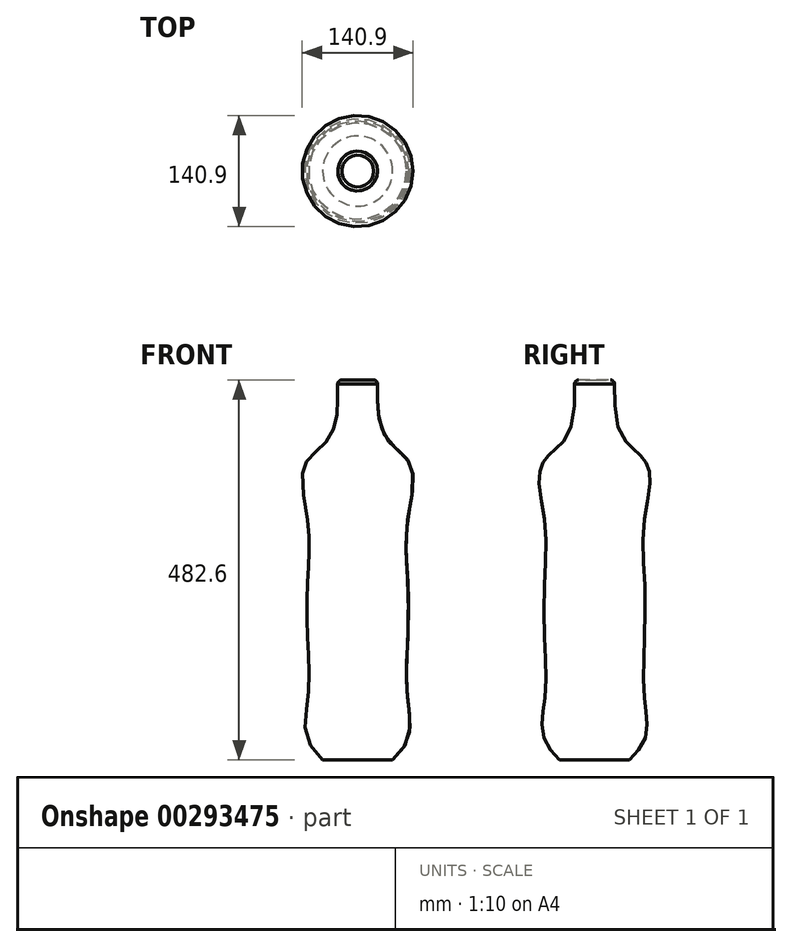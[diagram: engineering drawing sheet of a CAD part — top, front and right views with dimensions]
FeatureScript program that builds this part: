
annotation { "Feature Type Name" : "Feature", "Feature Type Description" : "" }
export const myFeature = defineFeature(function(context is Context, id is Id, definition is map)
    precondition{}
    {
        {
            var Q0;
            Q0=qCreatedBy(makeId("Top.planeOp"),FACE);
            cPlane(context, id + "F0", {"entities" : qUnion([Q0]), "cplaneType" : CPlaneType.OFFSET, "offset" : 76.2 * mm, "width" : 152.4 * mm, "height" : 152.4 * mm});
        }
        {
            var Q0;
            Q0=qCreatedBy(makeId("Top.planeOp"),FACE);
            cPlane(context, id + "F1", {"entities" : qUnion([Q0]), "cplaneType" : CPlaneType.OFFSET, "offset" : 228.6 * mm, "width" : 152.4 * mm, "height" : 152.4 * mm});
        }
        {
            var Q0;
            Q0=qCreatedBy(makeId("Top.planeOp"),FACE);
            cPlane(context, id + "F2", {"entities" : qUnion([Q0]), "cplaneType" : CPlaneType.OFFSET, "offset" : 152.4 * mm, "width" : 152.4 * mm, "height" : 152.4 * mm});
        }
        {
            var Q0;
            Q0=qCreatedBy(makeId("Top.planeOp"),FACE);
            cPlane(context, id + "F3", {"entities" : qUnion([Q0]), "cplaneType" : CPlaneType.OFFSET, "offset" : 304.8 * mm, "width" : 152.4 * mm, "height" : 152.4 * mm});
        }
        {
            var Q0;
            Q0=qCreatedBy(makeId("Top.planeOp"),FACE);
            cPlane(context, id + "F4", {"entities" : qUnion([Q0]), "cplaneType" : CPlaneType.OFFSET, "offset" : 381 * mm, "width" : 152.4 * mm, "height" : 152.4 * mm});
        }
        {
            var Q0;
            Q0=qCreatedBy(id+"F4.planeOp",FACE);
            cPlane(context, id + "F5", {"entities" : qUnion([Q0]), "cplaneType" : CPlaneType.OFFSET, "offset" : 76.2 * mm, "width" : 152.4 * mm, "height" : 152.4 * mm});
        }
        {
            var Q0;
            Q0=qCreatedBy(id+"F5.planeOp",FACE);
            cPlane(context, id + "F6", {"entities" : qUnion([Q0]), "cplaneType" : CPlaneType.OFFSET, "offset" : 76.2 * mm, "width" : 152.4 * mm, "height" : 152.4 * mm});
        }
        {
            var Q0;
            Q0=qCreatedBy(id+"F6.planeOp",FACE);
            cPlane(context, id + "F7", {"entities" : qUnion([Q0]), "cplaneType" : CPlaneType.OFFSET, "offset" : 76.2 * mm, "width" : 152.4 * mm, "height" : 152.4 * mm});
        }
        {
            var Q0;
            Q0=qCreatedBy(makeId("Top.planeOp"),FACE);
            cPlane(context, id + "F8", {"entities" : qUnion([Q0]), "cplaneType" : CPlaneType.OFFSET, "offset" : 25.4 * mm, "width" : 152.4 * mm, "height" : 152.4 * mm});
        }
        {
            var Q0;
            Q0=qCreatedBy(id+"F4.planeOp",FACE);
            cPlane(context, id + "F9", {"entities" : qUnion([Q0]), "cplaneType" : CPlaneType.OFFSET, "offset" : 25.4 * mm, "width" : 152.4 * mm, "height" : 152.4 * mm});
        }
        {
            var Q0;
            Q0=qCreatedBy(id+"F5.planeOp",FACE);
            cPlane(context, id + "F10", {"entities" : qUnion([Q0]), "cplaneType" : CPlaneType.OFFSET, "offset" : 25.4 * mm, "width" : 152.4 * mm, "height" : 152.4 * mm});
        }
        {
            var Q0;
            Q0=qCreatedBy(makeId("Top.planeOp"),FACE);
            var sketch = newSketch(context, id + "F11", { "sketchPlane" : qUnion([Q0])});
            skCircle(sketch, "E0", {"center": v(0, 0) * mm, "radius": 44.45 * mm});
            skSolve(sketch);
        }
        {
            var Q0;
            Q0=qCreatedBy(id+"F0.planeOp",FACE);
            var sketch = newSketch(context, id + "F12", { "sketchPlane" : qUnion([Q0])});
            skCircle(sketch, "E1", {"center": v(0, 0) * mm, "radius": 63.5 * mm});
            skSolve(sketch);
        }
        {
            var Q0;
            Q0=qCreatedBy(id+"F8.planeOp",FACE);
            var sketch = newSketch(context, id + "F13", { "sketchPlane" : qUnion([Q0])});
            skCircle(sketch, "E2", {"center": v(0, 0) * mm, "radius": 63.5 * mm});
            skSolve(sketch);
        }
        {
            var Q0;
            Q0=qCreatedBy(id+"F2.planeOp",FACE);
            var sketch = newSketch(context, id + "F14", { "sketchPlane" : qUnion([Q0])});
            skCircle(sketch, "E3", {"center": v(0, 0) * mm, "radius": 63.5 * mm});
            skSolve(sketch);
        }
        {
            var Q0;
            Q0=qCreatedBy(id+"F1.planeOp",FACE);
            var sketch = newSketch(context, id + "F15", { "sketchPlane" : qUnion([Q0])});
            skCircle(sketch, "E4", {"center": v(0, 0) * mm, "radius": 63.5 * mm});
            skSolve(sketch);
        }
        {
            var Q0;
            Q0=qCreatedBy(id+"F3.planeOp",FACE);
            var sketch = newSketch(context, id + "F16", { "sketchPlane" : qUnion([Q0])});
            skCircle(sketch, "E5", {"center": v(0, 0) * mm, "radius": 63.5 * mm});
            skSolve(sketch);
        }
        {
            var Q0;
            Q0=qCreatedBy(id+"F4.planeOp",FACE);
            var sketch = newSketch(context, id + "F17", { "sketchPlane" : qUnion([Q0])});
            skCircle(sketch, "E6", {"center": v(0, 0) * mm, "radius": 63.5 * mm});
            skSolve(sketch);
        }
        {
            var Q0;
            Q0=qCreatedBy(id+"F9.planeOp",FACE);
            var sketch = newSketch(context, id + "F18", { "sketchPlane" : qUnion([Q0])});
            skCircle(sketch, "E7", {"center": v(0, 0) * mm, "radius": 38.1 * mm});
            skSolve(sketch);
        }
        {
            var Q0;
            Q0=qCreatedBy(id+"F5.planeOp",FACE);
            var sketch = newSketch(context, id + "F19", { "sketchPlane" : qUnion([Q0])});
            skCircle(sketch, "E8", {"center": v(0, 0) * mm, "radius": 25.4 * mm});
            skSolve(sketch);
        }
        {
            var Q0;
            Q0=qCreatedBy(id+"F10.planeOp",FACE);
            var sketch = newSketch(context, id + "F20", { "sketchPlane" : qUnion([Q0])});
            skCircle(sketch, "E9", {"center": v(0, 0) * mm, "radius": 25.4 * mm});
            skSolve(sketch);
        }
        {
            var Q0;
            Q0=makeQuery(id+"F11.imprint","IMPRINT",FACE,{"disambiguationData":[TD([[makeQuery(id+"F11.imprint","IMPRINT",EDGE,{"derivedFrom":sQuery(id+"F11.wireOp",EDGE,"E0")}),1.0]])]});
            var Q1;
            Q1=makeQuery(id+"F13.imprint","IMPRINT",FACE,{"disambiguationData":[TD([[makeQuery(id+"F13.imprint","IMPRINT",EDGE,{"derivedFrom":sQuery(id+"F13.wireOp",EDGE,"E2")}),1.0]])]});
            var Q2;
            Q2=makeQuery(id+"F12.imprint","IMPRINT",FACE,{"disambiguationData":[TD([[makeQuery(id+"F12.imprint","IMPRINT",EDGE,{"derivedFrom":sQuery(id+"F12.wireOp",EDGE,"E1")}),1.0]])]});
            var Q3;
            Q3 = qSketchRegion(id + "F14", true);
            var Q4;
            Q4 = qSketchRegion(id + "F15", true);
            var Q5;
            Q5 = qSketchRegion(id + "F16", true);
            var Q6;
            Q6 = qSketchRegion(id + "F17", true);
            var Q7;
            Q7 = qSketchRegion(id + "F18", true);
            var Q8;
            Q8 = qSketchRegion(id + "F19", true);
            var Q9;
            Q9 = qSketchRegion(id + "F20", true);
            loft(context, id + "F21", {"sheetProfilesArray" : [{ "sheetProfileEntities" : qUnion([Q0]) }, { "sheetProfileEntities" : qUnion([Q1]) }, { "sheetProfileEntities" : qUnion([Q2]) }, { "sheetProfileEntities" : qUnion([Q3]) }, { "sheetProfileEntities" : qUnion([Q4]) }, { "sheetProfileEntities" : qUnion([Q5]) }, { "sheetProfileEntities" : qUnion([Q6]) }, { "sheetProfileEntities" : qUnion([Q7]) }, { "sheetProfileEntities" : qUnion([Q8]) }, { "sheetProfileEntities" : qUnion([Q9]) }]});
        }
        {
            var Q0;
            Q0=makeQuery(id+"F21.opLoft","MID_CAP_EDGE",EDGE,{"disambiguationData":[OSD([sQuery(id+"F11.wireOp",EDGE,"E0"),sQuery(id+"F20.wireOp",EDGE,"E9")])],"capPos":9.0});
            fillet(context, id + "F22", {"entities" : qUnion([Q0]), "radius" : 5.08 * mm, "tangentPropagation" : true, "allowEdgeOverflow" : false});
        }
    });
